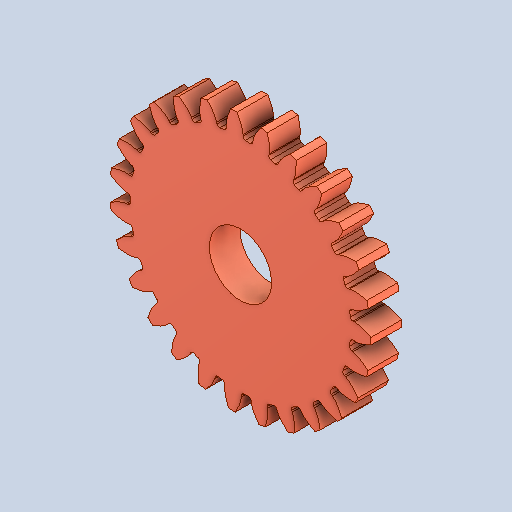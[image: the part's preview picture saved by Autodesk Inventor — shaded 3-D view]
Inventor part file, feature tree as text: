
AUTODESK INVENTOR PART (.ipt)
format: ipt  version: 2022 (Build 260153000, 153)  size: 462,848 bytes
history: imported  units: in
note: dims shown in document units (in); Inventor stores cm internally (conversion verified against a paired STEP export)
features: imported_body x1
ambient origin geometry x8: Origin, YZ Plane, XZ Plane, XY Plane, X Axis, Y Axis, Z Axis, Center Point
bodies: Solid1 (imported_parasolid), Body1 (imported_parasolid)
feature tree (1):
  imported_body  NMx_Import_Brep_tag  [imported B-rep: ~17 faces, bbox_mm=[14.284044, 9.199367, 3.1242]]
